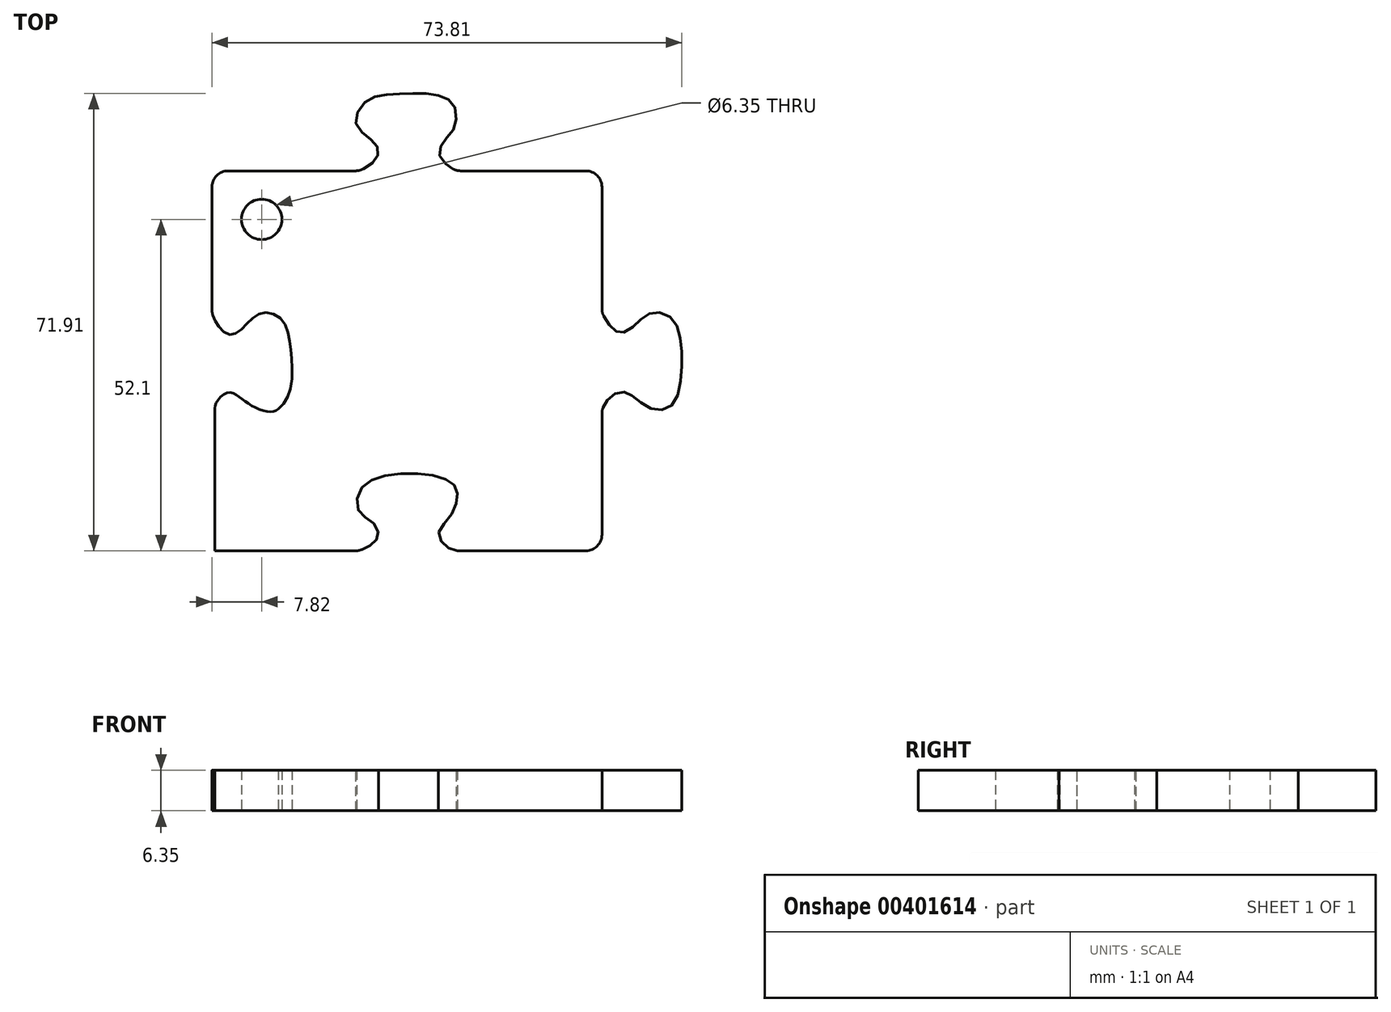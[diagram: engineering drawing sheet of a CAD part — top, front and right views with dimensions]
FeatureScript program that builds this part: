
annotation { "Feature Type Name" : "Feature", "Feature Type Description" : "" }
export const myFeature = defineFeature(function(context is Context, id is Id, definition is map)
    precondition{}
    {
        {
            var Q0;
            Q0=qCreatedBy(makeId("Top.planeOp"),FACE);
            var sketch = newSketch(context, id + "F0", { "sketchPlane" : qUnion([Q0])});
            skLineSegment(sketch, "E0.bottom", {"start": v(38.1, 38.1) * mm, "end": v(-38.1, 38.1) * mm, "construction": true});
            skLineSegment(sketch, "E0.top", {"start": v(38.1, -38.1) * mm, "end": v(-38.1, -38.1) * mm, "construction": true});
            skLineSegment(sketch, "E0.left", {"start": v(38.1, 38.1) * mm, "end": v(38.1, -38.1) * mm, "construction": true});
            skLineSegment(sketch, "E0.right", {"start": v(-38.1, 38.1) * mm, "end": v(-38.1, -38.1) * mm, "construction": true});
            skPoint(sketch, "E0.middle", {"position": v(0, 0) * mm});
            skLineSegment(sketch, "E1", {"start": v(-34.74, 25.07) * mm, "end": v(-14.72, 25.07) * mm});
            skLineSegment(sketch, "E2", {"start": v(1.8, 25.07) * mm, "end": v(21.44, 25.07) * mm});
            skLineSegment(sketch, "E3", {"start": v(23.98, 22.53) * mm, "end": v(23.98, 3.43) * mm});
            skLineSegment(sketch, "E4", {"start": v(23.98, -13.05) * mm, "end": v(23.98, -32.1) * mm});
            skLineSegment(sketch, "E5", {"start": v(21.44, -34.65) * mm, "end": v(1.58, -34.65) * mm});
            skLineSegment(sketch, "E6", {"start": v(-14.73, -34.65) * mm, "end": v(-36.83, -34.65) * mm});
            skLineSegment(sketch, "E7", {"start": v(-36.83, -34.65) * mm, "end": v(-36.83, -12.61) * mm});
            skLineSegment(sketch, "E8", {"start": v(-37.28, 22.53) * mm, "end": v(-37.28, 3.23) * mm});
            skFitSpline(sketch, "E9", {"points": [v(-37.28, 2.8) * mm, v(-36.64, 1.29) * mm, v(-35.04, -0.48) * mm, v(-33.35, -0.4) * mm, v(-31.2, 1.66) * mm, v(-28.94, 2.8) * mm, v(-26.31, 1.7) * mm, v(-25.12, -1.43) * mm, v(-24.7, -5.26) * mm, v(-25.16, -9.99) * mm, v(-26.89, -12.38) * mm], "startDerivative": vector(6.42, -18.91) * mm, "endDerivative": vector(-20.24, -18.94) * mm});
            skFitSpline(sketch, "E10", {"points": [v(-26.89, -12.38) * mm, v(-28.16, -12.79) * mm, v(-30.88, -11.92) * mm, v(-33.06, -10.4) * mm, v(-34.79, -9.78) * mm, v(-36.64, -11.43) * mm, v(-36.83, -12.61) * mm], "startDerivative": vector(-7.22, -6.07) * mm, "endDerivative": vector(0.38, -8.5) * mm});
            skFitSpline(sketch, "E11", {"points": [v(-14.1, 25.07) * mm, v(-11.66, 26.72) * mm, v(-11.17, 28.59) * mm, v(-12.9, 30.5) * mm, v(-14.68, 32.77) * mm, v(-13.17, 35.92) * mm, v(-9.97, 37.03) * mm, v(-5.62, 37.26) * mm, v(-1.48, 36.9) * mm, v(0.74, 35.39) * mm, v(0.87, 32.06) * mm, v(-0.64, 29.97) * mm, v(-1.57, 27.66) * mm, v(0, 25.74) * mm, v(1.21, 25.07) * mm], "startDerivative": vector(38.72, 19.86) * mm, "endDerivative": vector(22.38, -10.51) * mm});
            skArc(sketch, "E12.filletArc", {"start": v(-14.72, 25.07) * mm, "mid": v(-14.1, 25.15) * mm, "end": v(-13.53, 25.37) * mm});
            skArc(sketch, "E13.filletArc", {"start": v(0.58, 25.38) * mm, "mid": v(1.17, 25.15) * mm, "end": v(1.8, 25.07) * mm});
            skArc(sketch, "E14.filletArc", {"start": v(-37.28, 3.23) * mm, "mid": v(-37.24, 2.8) * mm, "end": v(-37.12, 2.36) * mm});
            skPoint(sketch, "E15.visualSharp", {"position": v(-37.28, 25.07) * mm});
            skArc(sketch, "E15.filletArc", {"start": v(-34.74, 25.07) * mm, "mid": v(-36.53, 24.33) * mm, "end": v(-37.28, 22.53) * mm});
            skPoint(sketch, "E16.visualSharp", {"position": v(23.98, 25.07) * mm});
            skArc(sketch, "E16.filletArc", {"start": v(23.98, 22.53) * mm, "mid": v(23.23, 24.33) * mm, "end": v(21.44, 25.07) * mm});
            skFitSpline(sketch, "E17", {"points": [v(23.98, 2.8) * mm, v(25.52, 0.39) * mm, v(27.2, -0.36) * mm, v(29.53, 1.22) * mm, v(31.86, 2.8) * mm, v(34.85, 1.93) * mm, v(36.35, -1.55) * mm, v(36.4, -7.14) * mm, v(35.03, -11.72) * mm, v(32.12, -12.42) * mm, v(29.09, -10.58) * mm, v(27.2, -9.65) * mm, v(24.9, -10.84) * mm, v(23.98, -12.6) * mm], "startDerivative": vector(18.91, -35.94) * mm, "endDerivative": vector(-10.25, -29.43) * mm});
            skArc(sketch, "E18.filletArc", {"start": v(23.98, 3.43) * mm, "mid": v(24.05, 2.8) * mm, "end": v(24.28, 2.22) * mm});
            skArc(sketch, "E19.filletArc", {"start": v(24.14, -12.14) * mm, "mid": v(24.02, -12.59) * mm, "end": v(23.98, -13.05) * mm});
            skPoint(sketch, "E20.visualSharp", {"position": v(23.98, -34.65) * mm});
            skArc(sketch, "E20.filletArc", {"start": v(21.44, -34.65) * mm, "mid": v(23.23, -33.9) * mm, "end": v(23.98, -32.1) * mm});
            skFitSpline(sketch, "E21", {"points": [v(-14.2, -34.65) * mm, v(-12.28, -33.67) * mm, v(-11.13, -32.16) * mm, v(-12.02, -30.22) * mm, v(-14.2, -28.43) * mm, v(-13.9, -24.94) * mm, v(-9.94, -22.83) * mm, v(-3.05, -22.72) * mm, v(0.61, -24.19) * mm, v(1.26, -26.2) * mm, v(0, -29.43) * mm, v(-1.68, -31.98) * mm, v(-0.32, -34.06) * mm, v(1.35, -34.65) * mm], "startDerivative": vector(30.63, 12.93) * mm, "endDerivative": vector(27.87, -5.12) * mm});
            skArc(sketch, "E22.filletArc", {"start": v(1.1, -34.6) * mm, "mid": v(1.34, -34.64) * mm, "end": v(1.58, -34.65) * mm});
            skArc(sketch, "E23.filletArc", {"start": v(-14.73, -34.65) * mm, "mid": v(-14.2, -34.6) * mm, "end": v(-13.7, -34.43) * mm});
            skLineSegment(sketch, "E24", {"start": v(-37.28, 25.07) * mm, "end": v(23.98, -34.65) * mm, "construction": true});
            skCircle(sketch, "E25", {"center": v(-29.46, 17.45) * mm, "radius": 3.18 * mm});
            skSolve(sketch);
        }
        {
            var Q0;
            Q0 = qSketchRegion(id + "F0", true);
            extrude(context, id + "F1", {"entities" : qUnion([Q0]), "depth" : 6.35 * mm});
        }
    });
